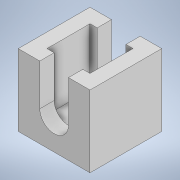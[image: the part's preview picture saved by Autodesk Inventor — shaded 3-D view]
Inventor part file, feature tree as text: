
AUTODESK INVENTOR PART (.ipt)
format: ipt  version: 2022 (Build 260153000, 153)  size: 110,080 bytes
history: native  units: in
note: dims shown in document units (in); Inventor stores cm internally (conversion verified against a paired STEP export)
features: extrude x2, sketch x2, shell x1
ambient origin geometry x8: Origin, YZ Plane, XZ Plane, XY Plane, X Axis, Y Axis, Z Axis, Center Point
bodies: Solid1 (feature_tree)
feature tree (5):
  extrude  "Extrusion1"  Depth=0.1969in
  shell  "Shell1"  Thickness=0.1969in
  extrude  "Extrusion3"  TaperAngle=0.0deg  [1 undecoded]
  sketch  "Sketch1"  dims[d0=0.1969in d1=0.1969in d2=0.1969in d3=0.0in]
  sketch  "Sketch3"  dims[d4=0.0394in d8=0.0in d9=0.0in]
note: 1 required parameter value undecoded (feature->parameter linkage not recoverable at this tier; creation-order binding heuristic only, values carry confidence <= 0.55)
